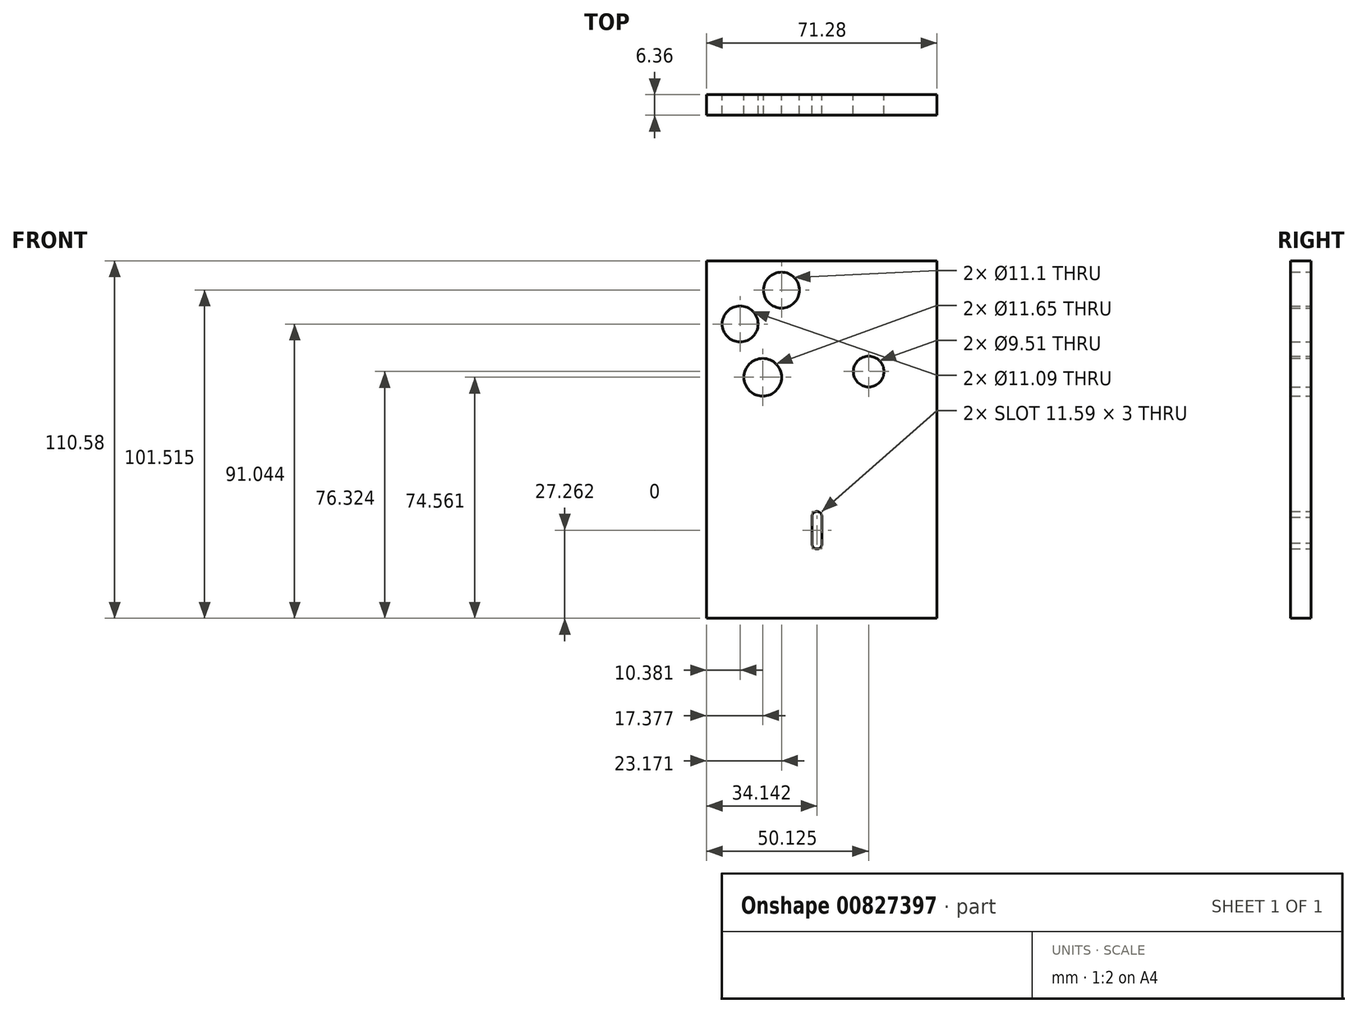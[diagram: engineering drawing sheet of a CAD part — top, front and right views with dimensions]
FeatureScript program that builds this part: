
annotation { "Feature Type Name" : "Feature", "Feature Type Description" : "" }
export const myFeature = defineFeature(function(context is Context, id is Id, definition is map)
    precondition{}
    {
        {
            var Q0;
            Q0=qCreatedBy(makeId("Front.planeOp"),FACE);
            var sketch = newSketch(context, id + "F0", { "sketchPlane" : qUnion([Q0])});
            skLineSegment(sketch, "E0.bottom", {"start": v(-35.64, 55.3) * mm, "end": v(35.64, 55.3) * mm});
            skLineSegment(sketch, "E0.top", {"start": v(-35.64, -55.3) * mm, "end": v(35.64, -55.3) * mm});
            skLineSegment(sketch, "E0.left", {"start": v(-35.64, 55.3) * mm, "end": v(-35.64, -55.3) * mm});
            skLineSegment(sketch, "E0.right", {"start": v(35.64, 55.3) * mm, "end": v(35.64, -55.3) * mm});
            skPoint(sketch, "E0.middle", {"position": v(0, 0) * mm});
            skCircle(sketch, "E1", {"center": v(-12.47, 46.23) * mm, "radius": 5.55 * mm});
            skCircle(sketch, "E2", {"center": v(-18.26, 19.27) * mm, "radius": 5.82 * mm});
            skCircle(sketch, "E3", {"center": v(14.48, 21.03) * mm, "radius": 4.75 * mm});
            skLineSegment(sketch, "E4.bottom", {"start": v(0, -23.98) * mm, "end": v(-3, -23.98) * mm});
            skLineSegment(sketch, "E4.top", {"start": v(0, -32.02) * mm, "end": v(-3, -32.02) * mm});
            skLineSegment(sketch, "E4.left", {"start": v(0, -23.98) * mm, "end": v(0, -32.02) * mm});
            skLineSegment(sketch, "E4.right", {"start": v(-3, -23.98) * mm, "end": v(-3, -32.02) * mm});
            skArc(sketch, "E5", {"start": v(0, -23.98) * mm, "mid": v(-1.5, -22.23) * mm, "end": v(-3, -23.98) * mm});
            skArc(sketch, "E6", {"start": v(-3, -32.02) * mm, "mid": v(-1.5, -33.82) * mm, "end": v(0, -32.02) * mm});
            skCircle(sketch, "E7", {"center": v(-25.26, 35.75) * mm, "radius": 5.54 * mm});
            skSolve(sketch);
        }
        {
            var Q0;
            Q0=makeQuery(id+"F0.imprint","IMPRINT",FACE,{"disambiguationData":[TD([[makeQuery(id+"F0.imprint","IMPRINT",EDGE,{"derivedFrom":sQuery(id+"F0.wireOp",EDGE,"E0.bottom")}),-1.0]])]});
            extrude(context, id + "F1", {"entities" : qUnion([Q0]), "endBound" : BoundingType.SYMMETRIC, "depth" : 6.35 * mm, "offsetDistance" : 25.4 * mm});
        }
        {
            var Q0;
            Q0 = qSketchRegion(id + "F0", true);
            extrude(context, id + "F2", {"entities" : qUnion([Q0]), "endBound" : BoundingType.SYMMETRIC, "depth" : 6.35 * mm, "offsetDistance" : 25.4 * mm});
        }
    });
